# Revit family: FU_Inspec_Grade_1-6
name_source: partatom
category: Furniture
units: mm (PartAtom-declared; Revit-internal decimal feet)

## family parameters
Always vertical = Yes
Cut with Voids When Loaded = No
OmniClass Number = 23.40.20.00
OmniClass Title = General Furniture and Specialties
Room Calculation Point = No
Shared = No
Work Plane-Based = No

## types (6) — shared parameters
Assembly Code = E2020
Depth = 780 mm  [stored 2.55906 ft]
Height = 540 mm  [stored 1.77165 ft]
Keynote = 46.B
Manufacturer = Inspec
URL = https://inspecfurniture.com
Weight = 4.7
Width = 480 mm  [stored 1.5748 ft]
zero-valued in all types: Default Elevation

## per-type parameters (varying)
| type | Description | Frame Material | Model | Seat Material | Seat Pad Material |
| Grade 1.4 - Ash - Blue green | Chair with recycled polypropylene seat on a wooden frame. | Wood - Solid - Ashtree | Grade 1.4 | Colour - Coated - Blue green | Fabric - Divina 3 - 384 |
| Grade 1.4 - Ash - White | Chair with recycled polypropylene seat on a wooden frame. | Wood - Solid - Ashtree | Grade 1.4 | Colour - Coated - White | Fabric - Divina 3 - 384 |
| Grade 1.5 - Black - Black | Chair with recycled polypropylene seat on a wooden frame with upholstered seat pad. | Colour - Coated - Black | Grade 1.5 | Colour - Coated - Black | Fabric - Divina Blue |
| Grade 1.5 - Ash - Blue | Chair with recycled polypropylene seat on a wooden frame with upholstered seat pad. | Wood - Solid - Ashtree | Grade 1.5 | Colour - Coated - Blue green | Fabric - Divina Blue |
| Grade 1.6 - Ash - Red | Chair with fully upholstered recycled polypropylene seat on a wooden frame | Wood - Solid - Ashtree | Grade 1.6 | Fabric - Divina Red | Fabric - Divina Blue |
| Grade 1.6 - Ash - Beige | Chair with fully upholstered recycled polypropylene seat on a wooden frame | Wood - Solid - Ashtree | Grade 1.6 | Fabric - Divina Beige | Fabric - Divina Blue |

note: [stored X ft] marks values corroborated as IEEE doubles in the binary element streams (Revit-internal decimal feet)

## geometry (parser evidence)
native form markers: Blend x451, Sweep x2
no freeform markers — native parametric forms only
